# Revit family: Legrand_Lighting_Management_Actuator
name_source: partatom
category: Dispositifs d'éclairage
units: mm (PartAtom-declared; Revit-internal decimal feet)

## family parameters
Conserver l'orientation des annotations = Non
Cote de connecteur circulaire = Utiliser le diamètre
Couper avec des vides une fois chargée = Non
Hôte = Face
Partagée = Non
Point de calcul de pièce = Non
Type d'élément = Normal

## types (3) — shared parameters
Alarm function = Non
Collecteur de terre = Non
Colour = <Par catégorie>
Constant light control = Non
Cosses d'artère secondaire = Non
Dim function with dimmer basic element = Non
Elévation par défaut = 1219 mm
Fabricant = Legrand
Forced switch off = Non
Frequency (MAX) (Hz) = 60
Frequency (MIN) (Hz) = 50
General Conditions of Use = https://export.legrand.com
HVAC-control = Non
Liaison neutre = Non
Mounting method = Surface mounted (plaster)
Nominal voltage (V) = 230
Remote operation = Non
Response value luminosity adjustable = Non
Response value sensitivity adjustable = Non
Substation input = Oui
Suitable for wireless transmission = Non
URL = http://www.legrandoc.com
zero-valued in all types: Detection angle horizontal (MAX) (°), Detection angle horizontal (MIN) (°), Diameter detection range on floor (m), Max. duty cycle (mn), Max. starting current (A), Max. switching power (W), Max. transmission range frontally (m), Max. transmission range sideways (m), Maximum mounting height (m), Min. switch-on time (s), RAL-number (akin), Response value luminosity (MAX) (lx), Response value luminosity (MIN) (lx), Temperature (MAX) (°C), Temperature (MIN) (°C)

## per-type parameters (varying)
| type | Description | Modèle |
| ON/OFF | Lighting management-power pack-ceiling mounting-2 outputs-1x16 A+dry contact | 048850 |
| DALI | Room controller for DALI and DSI dimming - 1 input - 2 outputs | 048851 |
| 0-10V | Dimming lighting controlller - 1 input-2 outputs 1-10 V | 048852 |
